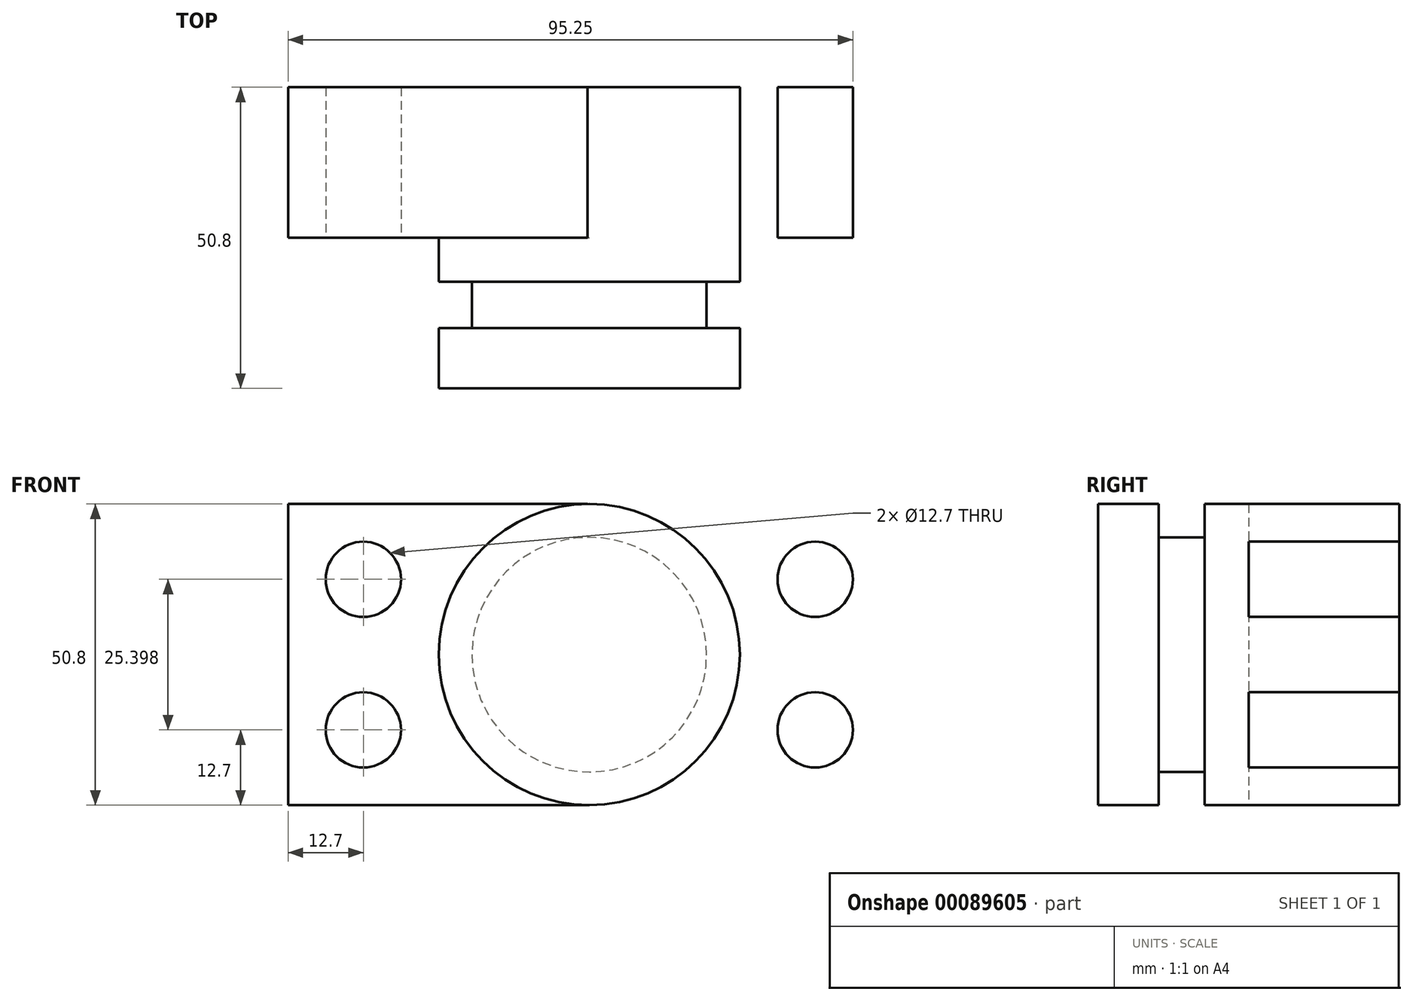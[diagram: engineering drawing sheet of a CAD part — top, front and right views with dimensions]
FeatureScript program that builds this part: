
annotation { "Feature Type Name" : "Feature", "Feature Type Description" : "" }
export const myFeature = defineFeature(function(context is Context, id is Id, definition is map)
    precondition{}
    {
        {
            var Q0;
            Q0=qCreatedBy(makeId("Front.planeOp"),FACE);
            var sketch = newSketch(context, id + "F0", { "sketchPlane" : qUnion([Q0])});
            skLineSegment(sketch, "E0", {"start": v(-50.8, 25.4) * mm, "end": v(50.8, 25.4) * mm});
            skLineSegment(sketch, "E1", {"start": v(-50.8, 25.4) * mm, "end": v(-50.8, -25.4) * mm});
            skLineSegment(sketch, "E2", {"start": v(-50.8, -25.4) * mm, "end": v(51.25, -25.4) * mm});
            skLineSegment(sketch, "E3", {"start": v(50.8, 25.4) * mm, "end": v(51.25, -25.4) * mm});
            skSolve(sketch);
        }
        {
            var Q0;
            Q0=makeQuery(id+"F0.imprint","IMPRINT",FACE,{"disambiguationData":[TD([[makeQuery(id+"F0.imprint","IMPRINT",EDGE,{"derivedFrom":sQuery(id+"F0.wireOp",EDGE,"E0")}),-1.0]])]});
            extrude(context, id + "F1", {"entities" : qUnion([Q0]), "depth" : 25.4 * mm});
        }
        {
            var Q0;
            Q0=makeQuery(id+"F1.opExtrude","CAP_FACE",FACE,{"disambiguationData":[OSD([sQuery(id+"F0.wireOp",EDGE,"E0"),sQuery(id+"F0.wireOp",EDGE,"E1"),sQuery(id+"F0.wireOp",EDGE,"E2"),sQuery(id+"F0.wireOp",EDGE,"E3")])],"isStart":false});
            var sketch = newSketch(context, id + "F2", { "sketchPlane" : qUnion([Q0])});
            skCircle(sketch, "E4", {"center": v(-38.1, 12.7) * mm, "radius": 6.35 * mm});
            skCircle(sketch, "E5", {"center": v(-38.1, -12.7) * mm, "radius": 6.35 * mm});
            skLineSegment(sketch, "E6", {"start": v(0, 25.4) * mm, "end": v(0, -25.4) * mm});
            skLineSegment(sketch, "E7", {"start": v(0, -25.4) * mm, "end": v(0, -25.4) * mm});
            skLineSegment(sketch, "E8", {"start": v(0, -25.4) * mm, "end": v(0, 25.4) * mm, "construction": true});
            skCircle(sketch, "E9.MirrorC", {"center": v(38.1, 12.7) * mm, "radius": 6.35 * mm});
            skCircle(sketch, "E10.MirrorC", {"center": v(38.1, -12.7) * mm, "radius": 6.35 * mm});
            skSolve(sketch);
        }
        {
            var Q0;
            Q0=makeQuery(id+"F2.imprint","IMPRINT",FACE,{"disambiguationData":[TD([[makeQuery(id+"F2.imprint","IMPRINT",EDGE,{"derivedFrom":sQuery(id+"F2.wireOp",EDGE,"E4")}),1.0]])]});
            var Q1;
            Q1=makeQuery(id+"F2.imprint","IMPRINT",FACE,{"disambiguationData":[TD([[makeQuery(id+"F2.imprint","IMPRINT",EDGE,{"derivedFrom":sQuery(id+"F2.wireOp",EDGE,"E5")}),1.0]])]});
            var Q2;
            Q2=makeQuery(id+"F2.imprint","IMPRINT",FACE,{"disambiguationData":[TD([[makeQuery(id+"F2.imprint","IMPRINT",EDGE,{"derivedFrom":sQuery(id+"F2.wireOp",EDGE,"E9.MirrorC")}),-1.0]])]});
            var Q3;
            Q3=makeQuery(id+"F2.imprint","IMPRINT",FACE,{"disambiguationData":[TD([[makeQuery(id+"F2.imprint","IMPRINT",EDGE,{"derivedFrom":sQuery(id+"F2.wireOp",EDGE,"E10.MirrorC")}),-1.0]])]});
            extrude(context, id + "F3", {"entities" : qUnion([Q0, Q1, Q2, Q3]), "operationType" : NewBodyOperationType.REMOVE, "endBound" : BoundingType.THROUGH_ALL, "oppositeDirection" : true, "depth" : 25.4 * mm});
        }
        {
            var Q0;
            Q0=qCreatedBy(makeId("Top.planeOp"),FACE);
            var sketch = newSketch(context, id + "F4", { "sketchPlane" : qUnion([Q0])});
            skLineSegment(sketch, "E11.bottom", {"start": v(0, 0) * mm, "end": v(25.4, 0) * mm});
            skLineSegment(sketch, "E11.top", {"start": v(0, -50.8) * mm, "end": v(25.4, -50.8) * mm});
            skLineSegment(sketch, "E11.left", {"start": v(0, 0) * mm, "end": v(0, -50.8) * mm});
            skLineSegment(sketch, "E11.right", {"start": v(25.4, 0) * mm, "end": v(25.4, -50.8) * mm});
            skSolve(sketch);
        }
        {
            var Q0;
            Q0=makeQuery(id+"F4.imprint","IMPRINT",FACE,{"disambiguationData":[TD([[makeQuery(id+"F4.imprint","IMPRINT",EDGE,{"derivedFrom":sQuery(id+"F4.wireOp",EDGE,"E11.bottom")}),-1.0]])]});
            var Q1;
            Q1=sQuery(id+"F4.wireOp",EDGE,"E11.left");
            revolve(context, id + "F5", {"operationType" : NewBodyOperationType.ADD, "entities" : qUnion([Q0]), "axis" : qUnion([Q1]), "revolveType" : RevolveType.FULL});
        }
        {
            var Q0;
            Q0=qCreatedBy(makeId("Top.planeOp"),FACE);
            var sketch = newSketch(context, id + "F6", { "sketchPlane" : qUnion([Q0])});
            skLineSegment(sketch, "E12", {"start": v(0, 0) * mm, "end": v(0, -49.88) * mm, "construction": true});
            skLineSegment(sketch, "E13", {"start": v(25.4, -32.83) * mm, "end": v(25.4, -40.6) * mm});
            skLineSegment(sketch, "E14", {"start": v(25.4, -40.6) * mm, "end": v(19.79, -40.6) * mm});
            skLineSegment(sketch, "E15", {"start": v(19.79, -40.6) * mm, "end": v(19.79, -32.83) * mm});
            skLineSegment(sketch, "E16", {"start": v(25.4, -32.83) * mm, "end": v(19.79, -32.83) * mm});
            skSolve(sketch);
        }
        {
            var Q0;
            Q0 = qSketchRegion(id + "F6", true);
            var Q1;
            Q1=sQuery(id+"F6.wireOp",EDGE,"E12");
            revolve(context, id + "F7", {"operationType" : NewBodyOperationType.REMOVE, "entities" : qUnion([Q0]), "axis" : qUnion([Q1]), "revolveType" : RevolveType.FULL, "oppositeDirection" : true});
        }
    });
